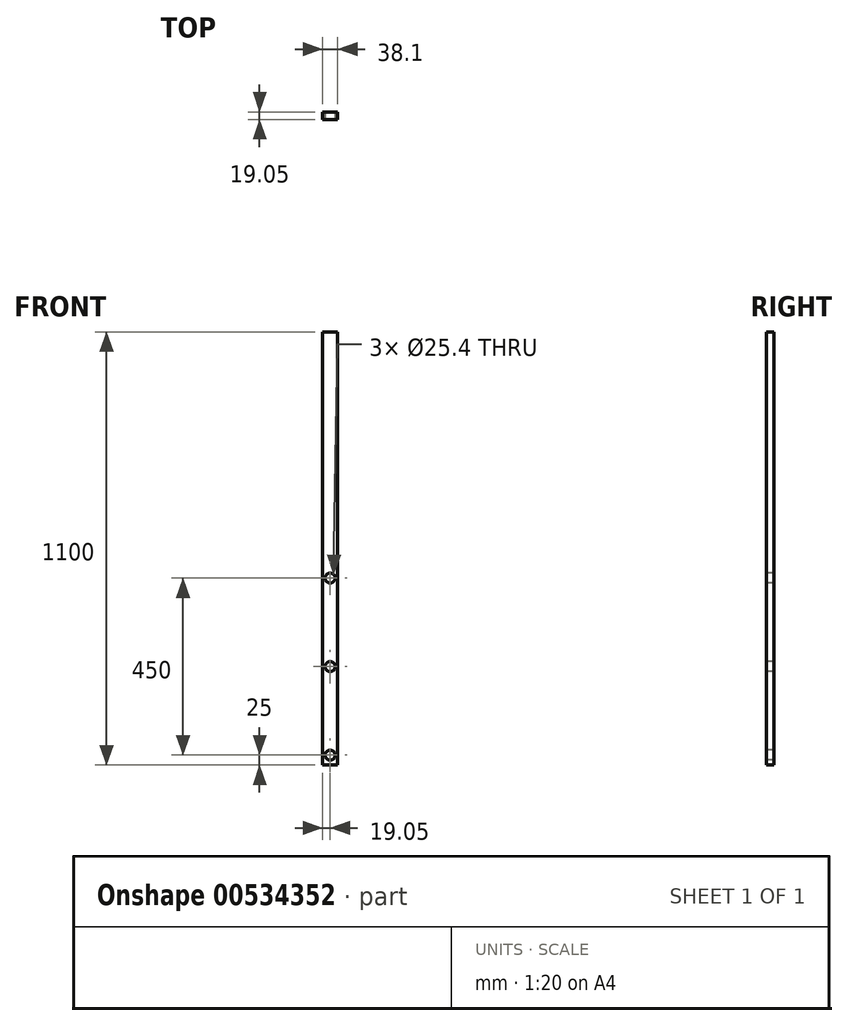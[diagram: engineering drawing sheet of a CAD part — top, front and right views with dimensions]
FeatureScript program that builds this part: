
annotation { "Feature Type Name" : "Feature", "Feature Type Description" : "" }
export const myFeature = defineFeature(function(context is Context, id is Id, definition is map)
    precondition{}
    {
        {
            var Q0;
            Q0=qCreatedBy(makeId("Front.planeOp"),FACE);
            var sketch = newSketch(context, id + "F0", { "sketchPlane" : qUnion([Q0])});
            skLineSegment(sketch, "E0", {"start": v(0, 0) * mm, "end": v(0, 500) * mm});
            skLineSegment(sketch, "E1", {"start": v(0, 500) * mm, "end": v(38.1, 500) * mm});
            skLineSegment(sketch, "E2", {"start": v(38.1, 500) * mm, "end": v(38.1, 0) * mm});
            skLineSegment(sketch, "E3", {"start": v(38.1, 0) * mm, "end": v(0, 0) * mm});
            skSolve(sketch);
        }
        {
            var Q0;
            Q0=makeQuery(id+"F0.imprint","IMPRINT",FACE,{"disambiguationData":[TD([[makeQuery(id+"F0.imprint","IMPRINT",EDGE,{"derivedFrom":sQuery(id+"F0.wireOp",EDGE,"E0")}),-1.0]])]});
            extrude(context, id + "F1", {"entities" : qUnion([Q0]), "depth" : 19.05 * mm, "offsetDistance" : 25 * mm});
        }
        {
            var Q0;
            Q0=makeQuery(id+"F1.opExtrude","CAP_FACE",FACE,{"disambiguationData":[OSD([sQuery(id+"F0.wireOp",EDGE,"E0"),sQuery(id+"F0.wireOp",EDGE,"E1"),sQuery(id+"F0.wireOp",EDGE,"E2"),sQuery(id+"F0.wireOp",EDGE,"E3")])],"isStart":false});
            var sketch = newSketch(context, id + "F2", { "sketchPlane" : qUnion([Q0])});
            skCircle(sketch, "E4", {"center": v(19.05, 475) * mm, "radius": 12.7 * mm});
            skCircle(sketch, "E5", {"center": v(19.05, 25) * mm, "radius": 12.7 * mm});
            skLineSegment(sketch, "E6", {"start": v(19.05, 25) * mm, "end": v(19.05, 0) * mm, "construction": true});
            skLineSegment(sketch, "E7", {"start": v(19.05, 475) * mm, "end": v(19.05, 500) * mm, "construction": true});
            skSolve(sketch);
        }
        {
            var Q0;
            Q0=makeQuery(id+"F2.imprint","IMPRINT",FACE,{"disambiguationData":[TD([[makeQuery(id+"F2.imprint","IMPRINT",EDGE,{"derivedFrom":sQuery(id+"F2.wireOp",EDGE,"E4")}),1.0]])]});
            var Q1;
            Q1=makeQuery(id+"F2.imprint","IMPRINT",FACE,{"disambiguationData":[TD([[makeQuery(id+"F2.imprint","IMPRINT",EDGE,{"derivedFrom":sQuery(id+"F2.wireOp",EDGE,"E5")}),1.0]])]});
            extrude(context, id + "F3", {"entities" : qUnion([Q0, Q1]), "operationType" : NewBodyOperationType.REMOVE, "oppositeDirection" : true, "depth" : 25 * mm, "offsetDistance" : 25 * mm});
        }
        {
            var Q0;
            Q0=makeQuery(id+"F1.opExtrude","CAP_FACE",FACE,{"disambiguationData":[OSD([sQuery(id+"F0.wireOp",EDGE,"E0"),sQuery(id+"F0.wireOp",EDGE,"E1"),sQuery(id+"F0.wireOp",EDGE,"E2"),sQuery(id+"F0.wireOp",EDGE,"E3")])],"isStart":false});
            var sketch = newSketch(context, id + "F4", { "sketchPlane" : qUnion([Q0])});
            skCircle(sketch, "E8", {"center": v(19.05, 250) * mm, "radius": 12.7 * mm});
            skPoint(sketch, "E9", {"position": v(19.05, 0) * mm});
            skSolve(sketch);
        }
        {
            var Q0;
            Q0=makeQuery(id+"F4.imprint","IMPRINT",FACE,{"disambiguationData":[TD([[makeQuery(id+"F4.imprint","IMPRINT",EDGE,{"derivedFrom":sQuery(id+"F4.wireOp",EDGE,"E8")}),1.0]])]});
            extrude(context, id + "F5", {"entities" : qUnion([Q0]), "operationType" : NewBodyOperationType.REMOVE, "oppositeDirection" : true, "depth" : 25 * mm, "offsetDistance" : 25 * mm});
        }
        {
            var Q0;
            Q0=makeQuery(id+"F1.opExtrude","SWEPT_FACE",FACE,{"disambiguationData":[OSD([sQuery(id+"F0.wireOp",EDGE,"E1")])]});
            var sketch = newSketch(context, id + "F6", { "sketchPlane" : qUnion([Q0])});
            skLineSegment(sketch, "E10.bottom", {"start": v(0, 0) * mm, "end": v(38.1, 0) * mm});
            skLineSegment(sketch, "E10.top", {"start": v(0, -19.05) * mm, "end": v(38.1, -19.05) * mm});
            skLineSegment(sketch, "E10.left", {"start": v(0, 0) * mm, "end": v(0, -19.05) * mm});
            skLineSegment(sketch, "E10.right", {"start": v(38.1, 0) * mm, "end": v(38.1, -19.05) * mm});
            skSolve(sketch);
        }
        {
            var Q0;
            Q0 = qSketchRegion(id + "F6", true);
            extrude(context, id + "F7", {"entities" : qUnion([Q0]), "operationType" : NewBodyOperationType.ADD, "depth" : 600 * mm, "offsetDistance" : 25 * mm});
        }
    });
